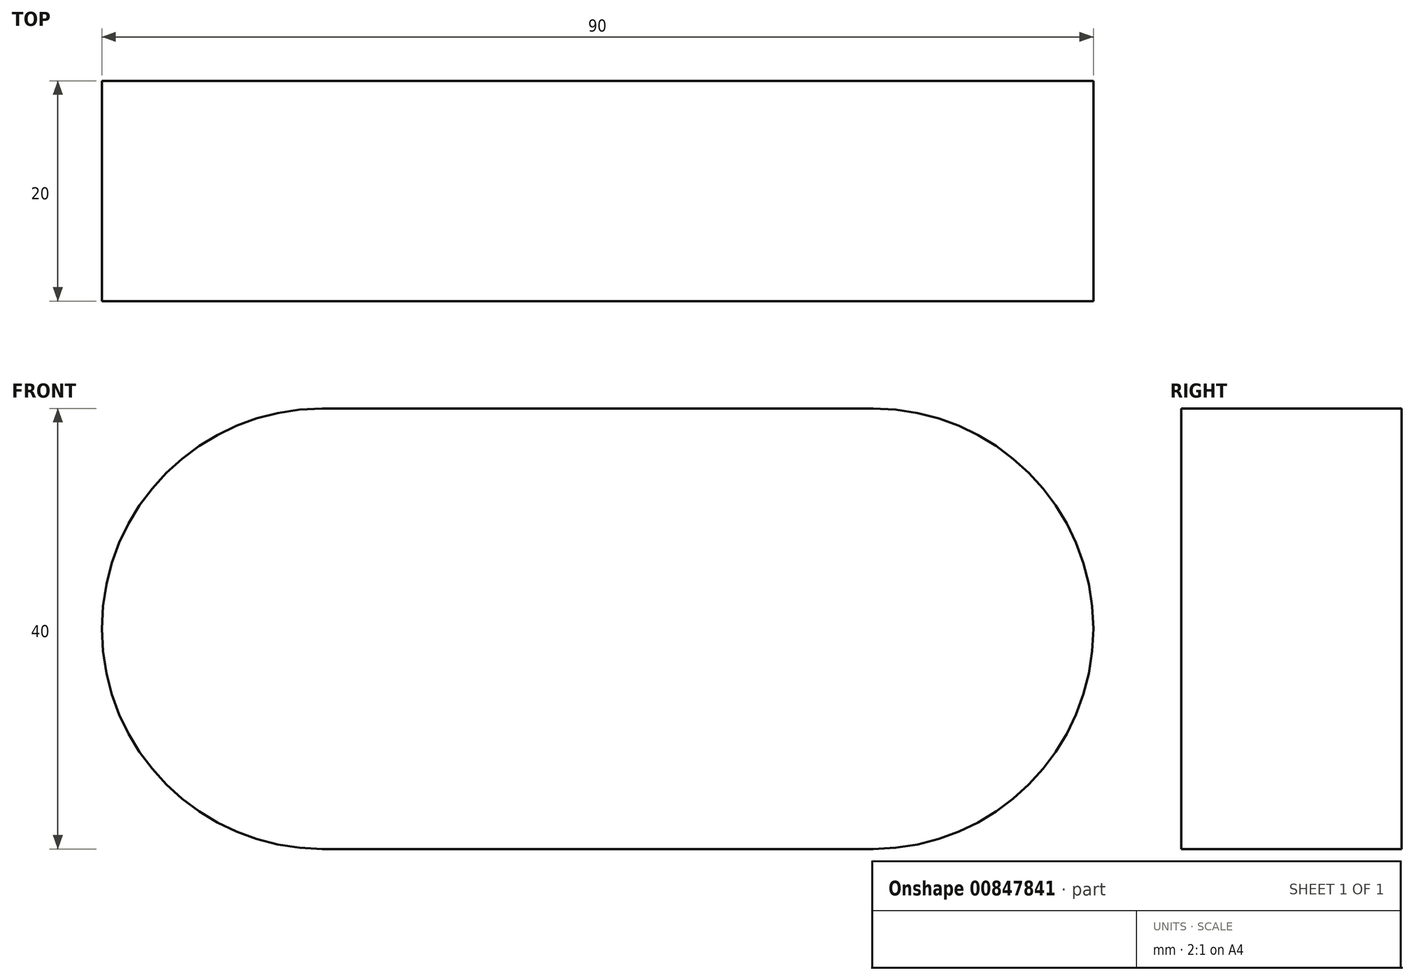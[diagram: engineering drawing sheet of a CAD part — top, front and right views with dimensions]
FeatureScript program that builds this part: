
annotation { "Feature Type Name" : "Feature", "Feature Type Description" : "" }
export const myFeature = defineFeature(function(context is Context, id is Id, definition is map)
    precondition{}
    {
        {
            var Q0;
            Q0=qCreatedBy(makeId("Front.planeOp"),FACE);
            var sketch = newSketch(context, id + "F0", { "sketchPlane" : qUnion([Q0])});
            skLineSegment(sketch, "E0.bottom", {"start": v(-25, 20) * mm, "end": v(25, 20) * mm});
            skLineSegment(sketch, "E0.top", {"start": v(-25, -20) * mm, "end": v(25, -20) * mm});
            skLineSegment(sketch, "E0.left", {"start": v(-25, 20) * mm, "end": v(-25, -20) * mm});
            skLineSegment(sketch, "E0.right", {"start": v(25, 20) * mm, "end": v(25, -20) * mm});
            skCircle(sketch, "E1", {"center": v(25, 0) * mm, "radius": 20 * mm});
            skCircle(sketch, "E2", {"center": v(-25, 0) * mm, "radius": 20 * mm});
            skPoint(sketch, "E3", {"position": v(-45, 0) * mm});
            skPoint(sketch, "E4", {"position": v(45, 0) * mm});
            skLineSegment(sketch, "E5", {"start": v(-19.8, 0) * mm, "end": v(29.78, 0) * mm, "construction": true});
            skPoint(sketch, "E6", {"position": v(0, 20) * mm});
            skLineSegment(sketch, "E7", {"start": v(0, 31.27) * mm, "end": v(0, -39.69) * mm, "construction": true});
            skSolve(sketch);
        }
        {
            var Q0;
            Q0 = qSketchRegion(id + "F0", true);
            extrude(context, id + "F1", {"entities" : qUnion([Q0]), "endBound" : BoundingType.SYMMETRIC, "depth" : 20 * mm, "offsetDistance" : 25 * mm});
        }
    });
